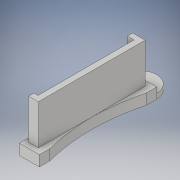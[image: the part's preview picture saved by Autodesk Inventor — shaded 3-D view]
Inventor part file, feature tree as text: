
AUTODESK INVENTOR PART (.ipt)
format: ipt  version: 2018 (Build 220112000, 112)  size: 136,704 bytes
history: native  units: in
note: dims shown in document units (in); Inventor stores cm internally (conversion verified against a paired STEP export)
features: extrude x3, sketch x3
ambient origin geometry x8: Origin, YZ Plane, XZ Plane, XY Plane, X Axis, Y Axis, Z Axis, Center Point
bodies: Solid1 (feature_tree)
feature tree (6):
  extrude  "Extrusion1"  Depth=0.1969in
  extrude  "Extrusion2"  Depth=2.7559in
  extrude  "Extrusion3"  Depth=0.2953in
  sketch  "Sketch1"  dims[d0=1.4173in d1=0.1969in]
  sketch  "Sketch2"  dims[d4=0.4724in d6=2.7559in]
  sketch  "Sketch3"  dims[d7=0.1575in d8=0.2953in d11=0.1575in d12=0.0in d13=0.0787in d14=0.0in d15=0.0787in d17=0.0787in d18=0.5906in d19=0.0in d20=1.1811in]
